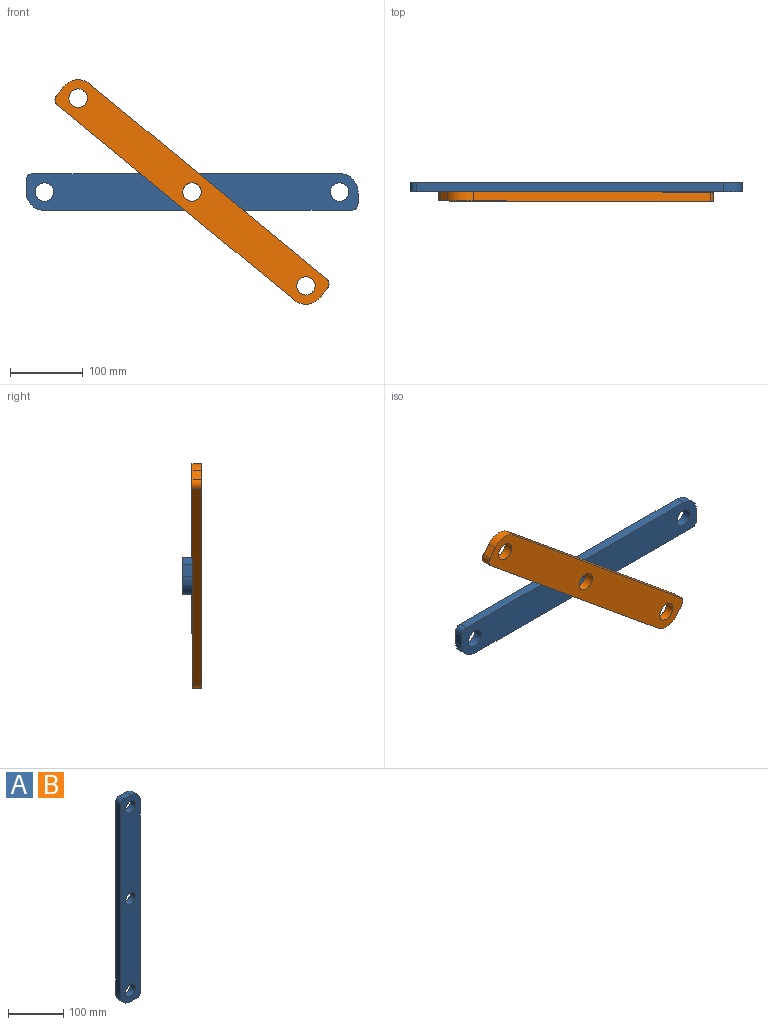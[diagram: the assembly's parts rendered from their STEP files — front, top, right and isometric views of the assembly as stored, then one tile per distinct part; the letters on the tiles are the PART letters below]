
ASSEMBLY  parts=2 mates=1
PART A: 13 faces, bbox 50.8x12.7x457.2 mm
  f0: plane 422.28x12.7mm, normal (-1,0,0), area 5362.9mm2, adj f1,f8,f11,f12
  f1: cylinder r=25.4mm len=25.4mm, axis (0,1,0), area 506.7mm2, adj f0,f2,f11,f12
  f2: plane 15.88x12.7mm, normal (0,0,-1), area 201.6mm2, adj f1,f3,f11,f12
  f3: cylinder r=9.53mm len=12.7mm, axis (0,1,0), area 190mm2, adj f2,f4,f11,f12
  f4: plane 422.28x12.7mm, normal (1,0,0), area 5362.9mm2, adj f3,f5,f11,f12
  f5: cylinder r=25.4mm len=25.4mm, axis (0,1,0), area 506.7mm2, adj f4,f6,f11,f12
  f6: plane 15.88x12.7mm, normal (0,0,1), area 201.6mm2, adj f5,f8,f11,f12
  f7: cylinder r=12.7mm len=25.4mm, axis (0,1,0), area 1013.4mm2, adj f11,f12
  f8: cylinder r=9.53mm len=12.7mm, axis (0,1,0), area 190mm2, adj f0,f6,f11,f12
  f9: cylinder r=12.7mm len=25.4mm, axis (0,1,0), area 1013.4mm2, adj f11,f12
  f10: cylinder r=12.7mm len=25.4mm, axis (0,1,0), area 1013.4mm2, adj f11,f12
  f11: plane 457.2x50.8mm, normal (0,-1,0), area 21389.8mm2, adj f0,f1,f2,f3,f4,f5,f6,f7
  f12: plane 457.2x50.8mm, normal (0,1,0), area 21389.8mm2, adj f0,f1,f2,f3,f4,f5,f6,f7
PART B: same geometry as A
PLACE A rot(axis=(-0.71,0,-0.71),180deg) t=(0,12.7,0)mm
PLACE B rot(axis=(0,-1,0),50.5deg) t=(0,0,0)mm
MATE revolute A.f9 <-> B.f9  axis (0,-1,0) through (0,6.35,0)mm
